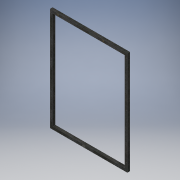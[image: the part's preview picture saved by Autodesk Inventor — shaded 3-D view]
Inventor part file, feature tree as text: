
AUTODESK INVENTOR PART (.ipt)
format: ipt  version: 2019 (Build 230136000, 136)  size: 108,544 bytes
history: native  units: mm
features: extrude x1, sketch x1
ambient origin geometry x8: Origin, YZ Plane, XZ Plane, XY Plane, X Axis, Y Axis, Z Axis, Center Point
bodies: Solid1 (feature_tree)
feature tree (2):
  extrude  "Extrusion1"  Depth=10.0mm
  sketch  "Sketch1"  dims[d0=300.0mm d1=10.0mm d2=10.0mm d3=10.0mm d4=10.0mm d5=400.0mm d6=172.5mm d7=115.0mm d8=10.0mm d9=0.0mm]
